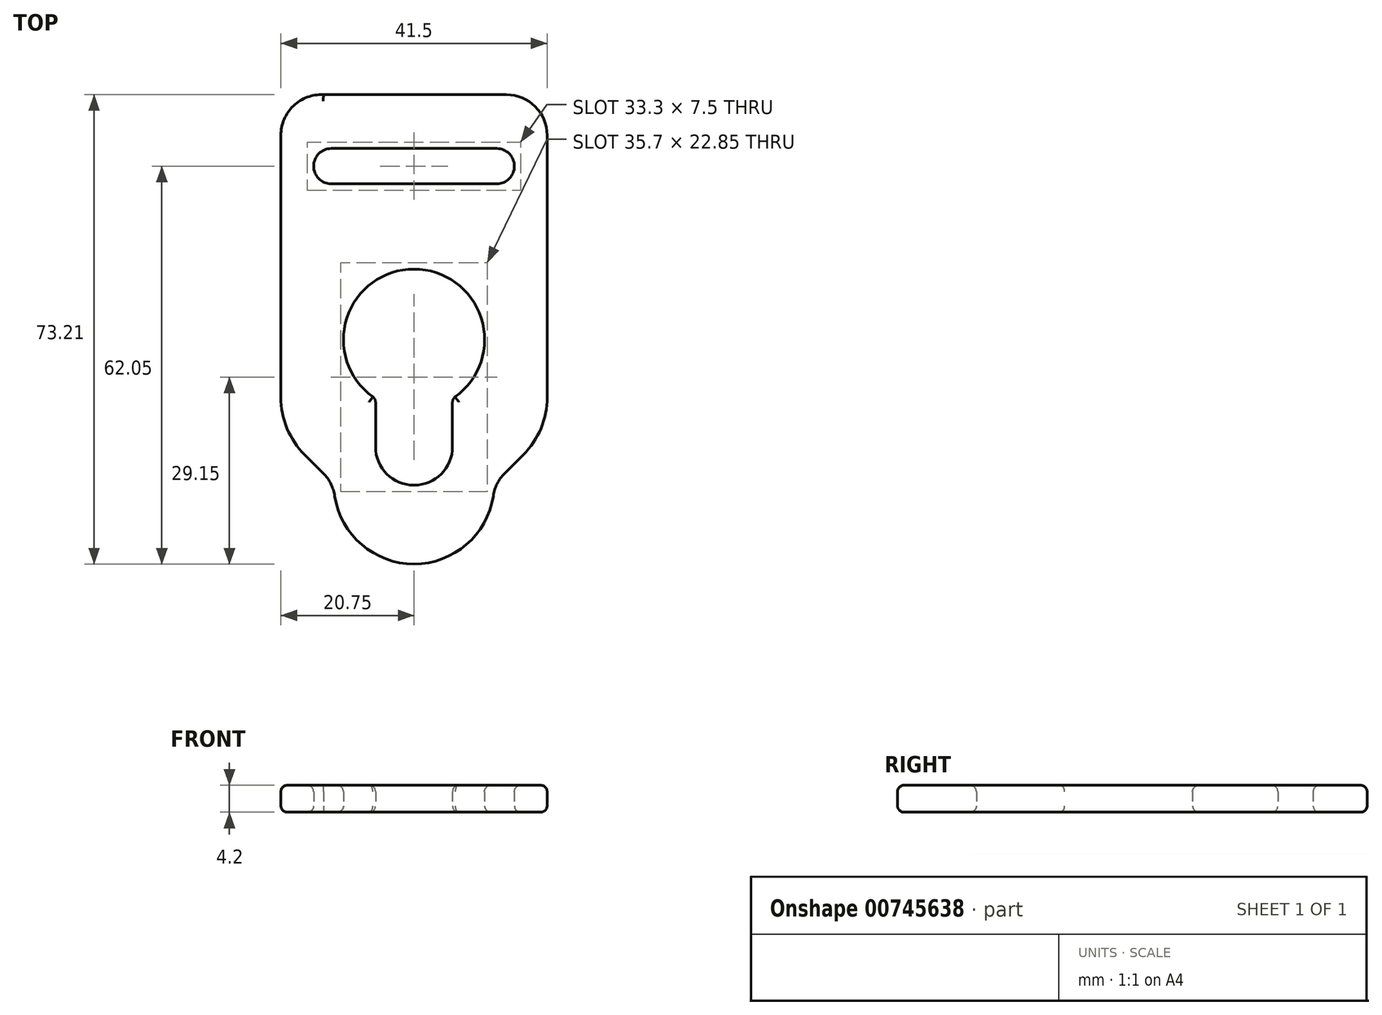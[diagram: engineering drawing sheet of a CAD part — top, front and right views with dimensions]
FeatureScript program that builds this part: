
annotation { "Feature Type Name" : "Feature", "Feature Type Description" : "" }
export const myFeature = defineFeature(function(context is Context, id is Id, definition is map)
    precondition{}
    {
        {
            var Q0;
            Q0=qCreatedBy(makeId("Top.planeOp"),FACE);
            var sketch = newSketch(context, id + "F0", { "sketchPlane" : qUnion([Q0])});
            skLineSegment(sketch, "E0.bottom", {"start": v(0, 0) * mm, "end": v(14.4, 0) * mm});
            skLineSegment(sketch, "E0.right", {"start": v(20.75, -6.35) * mm, "end": v(20.75, -47.19) * mm});
            skArc(sketch, "E1.filletArc", {"start": v(20.75, -6.35) * mm, "mid": v(18.9, -1.86) * mm, "end": v(14.4, 0) * mm});
            skArc(sketch, "E2", {"start": v(0, -73.2) * mm, "mid": v(8.14, -70.18) * mm, "end": v(12.36, -62.59) * mm});
            skLineSegment(sketch, "E3", {"start": v(14.14, -59.06) * mm, "end": v(17.03, -56.17) * mm});
            skArc(sketch, "E4.filletArc", {"start": v(17.03, -56.17) * mm, "mid": v(19.78, -52.05) * mm, "end": v(20.75, -47.19) * mm});
            skPoint(sketch, "E5.visualSharp", {"position": v(12.5, -60.7) * mm});
            skArc(sketch, "E5.filletArc", {"start": v(14.14, -59.06) * mm, "mid": v(12.97, -60.68) * mm, "end": v(12.36, -62.59) * mm});
            skArc(sketch, "E6", {"start": v(0, -60.9) * mm, "mid": v(4.24, -59.14) * mm, "end": v(6, -54.9) * mm});
            skLineSegment(sketch, "E7", {"start": v(6, -54.9) * mm, "end": v(6, -47.42) * mm});
            skArc(sketch, "E8.trimOffspring", {"start": v(6, -47.42) * mm, "mid": v(10.55, -35.07) * mm, "end": v(0, -27.2) * mm});
            skLineSegment(sketch, "E9.MirrorCS", {"start": v(-14.14, -59.06) * mm, "end": v(-17.03, -56.17) * mm});
            skArc(sketch, "E10.MirrorCS", {"start": v(-14.14, -59.06) * mm, "mid": v(-12.97, -60.68) * mm, "end": v(-12.36, -62.59) * mm});
            skArc(sketch, "E11.MirrorCS", {"start": v(-20.75, -6.35) * mm, "mid": v(-18.8, -1.76) * mm, "end": v(-14.12, 0) * mm});
            skArc(sketch, "E12.MirrorCS", {"start": v(-17.03, -56.17) * mm, "mid": v(-19.78, -52.05) * mm, "end": v(-20.75, -47.19) * mm});
            skArc(sketch, "E13.MirrorCS", {"start": v(0, -73.2) * mm, "mid": v(-8.14, -70.18) * mm, "end": v(-12.36, -62.59) * mm});
            skPoint(sketch, "E14.MirrorP", {"position": v(-12.5, -60.7) * mm});
            skArc(sketch, "E15.MirrorCS", {"start": v(0, -60.9) * mm, "mid": v(-4.24, -59.14) * mm, "end": v(-6, -54.9) * mm});
            skLineSegment(sketch, "E16.MirrorCS", {"start": v(0.28, 0) * mm, "end": v(-14.12, 0) * mm});
            skArc(sketch, "E17.MirrorCS", {"start": v(-6, -47.42) * mm, "mid": v(-10.55, -35.07) * mm, "end": v(0, -27.2) * mm});
            skLineSegment(sketch, "E18.MirrorCS", {"start": v(-6, -54.9) * mm, "end": v(-6, -47.42) * mm});
            skLineSegment(sketch, "E19.MirrorCS", {"start": v(-20.75, -6.35) * mm, "end": v(-20.75, -47.19) * mm});
            skLineSegment(sketch, "E20.bottom", {"start": v(-12.9, -8.4) * mm, "end": v(12.9, -8.4) * mm});
            skLineSegment(sketch, "E20.top", {"start": v(-12.9, -13.9) * mm, "end": v(12.9, -13.9) * mm});
            skLineSegment(sketch, "E20.left", {"start": v(-15.65, -11.15) * mm, "end": v(-15.65, -11.15) * mm});
            skLineSegment(sketch, "E20.right", {"start": v(15.65, -11.15) * mm, "end": v(15.65, -11.15) * mm});
            skPoint(sketch, "E21.visualSharp", {"position": v(-15.65, -13.9) * mm});
            skArc(sketch, "E21.filletArc", {"start": v(-15.65, -11.15) * mm, "mid": v(-14.84, -13.1) * mm, "end": v(-12.9, -13.9) * mm});
            skPoint(sketch, "E22.visualSharp", {"position": v(15.65, -13.9) * mm});
            skArc(sketch, "E22.filletArc", {"start": v(12.9, -13.9) * mm, "mid": v(14.84, -13.1) * mm, "end": v(15.65, -11.15) * mm});
            skPoint(sketch, "E23.visualSharp", {"position": v(-15.65, -8.4) * mm});
            skArc(sketch, "E23.filletArc", {"start": v(-12.9, -8.4) * mm, "mid": v(-14.84, -9.2) * mm, "end": v(-15.65, -11.15) * mm});
            skPoint(sketch, "E24.visualSharp", {"position": v(15.65, -8.4) * mm});
            skArc(sketch, "E24.filletArc", {"start": v(15.65, -11.15) * mm, "mid": v(14.84, -9.2) * mm, "end": v(12.9, -8.4) * mm});
            skSolve(sketch);
        }
        {
            var Q0;
            Q0=makeQuery(id+"F0.imprint","IMPRINT",FACE,{"disambiguationData":[TD([[makeQuery(id+"F0.imprint","IMPRINT",EDGE,{"derivedFrom":sQuery(id+"F0.wireOp",EDGE,"E0.bottom")}),-1.0]])]});
            extrude(context, id + "F1", {"entities" : qUnion([Q0]), "depth" : 4.2 * mm, "offsetDistance" : 25 * mm});
        }
        {
            var Q0;
            Q0=makeQuery(id+"F1.opExtrude","CAP_EDGE",EDGE,{"disambiguationData":[OSD([sQuery(id+"F0.wireOp",EDGE,"E0.right")])],"isStart":false});
            var Q1;
            Q1=makeQuery(id+"F1.opExtrude","CAP_EDGE",EDGE,{"disambiguationData":[OSD([sQuery(id+"F0.wireOp",EDGE,"E0.right")])],"isStart":true});
            var Q2;
            Q2=makeQuery(id+"F1.opExtrude","CAP_EDGE",EDGE,{"disambiguationData":[OSD([sQuery(id+"F0.wireOp",EDGE,"E8.trimOffspring"),sQuery(id+"F0.wireOp",EDGE,"E17.MirrorCS")])],"isStart":false});
            var Q3;
            Q3=makeQuery(id+"F1.opExtrude","CAP_EDGE",EDGE,{"disambiguationData":[OSD([sQuery(id+"F0.wireOp",EDGE,"E18.MirrorCS")])],"isStart":false});
            var Q4;
            Q4=makeQuery(id+"F1.opExtrude","CAP_EDGE",EDGE,{"disambiguationData":[OSD([sQuery(id+"F0.wireOp",EDGE,"E8.trimOffspring"),sQuery(id+"F0.wireOp",EDGE,"E17.MirrorCS")])],"isStart":true});
            var Q5;
            Q5=makeQuery(id+"F1.opExtrude","CAP_EDGE",EDGE,{"disambiguationData":[OSD([sQuery(id+"F0.wireOp",EDGE,"E18.MirrorCS")])],"isStart":true});
            var Q6;
            Q6=makeQuery(id+"F1.opExtrude","SWEPT_EDGE",EDGE,{"disambiguationData":[OSD([sQuery(id+"F0.wireOp",EDGE,"E17.MirrorCS"),sQuery(id+"F0.wireOp",EDGE,"E18.MirrorCS")])]});
            var Q7;
            Q7=makeQuery(id+"F1.opExtrude","SWEPT_EDGE",EDGE,{"disambiguationData":[OSD([sQuery(id+"F0.wireOp",EDGE,"E7"),sQuery(id+"F0.wireOp",EDGE,"E8.trimOffspring")])]});
            var Q8;
            Q8=makeQuery(id+"F1.opExtrude","CAP_EDGE",EDGE,{"disambiguationData":[OSD([sQuery(id+"F0.wireOp",EDGE,"E20.bottom")])],"isStart":false});
            var Q9;
            Q9=makeQuery(id+"F1.opExtrude","CAP_EDGE",EDGE,{"disambiguationData":[OSD([sQuery(id+"F0.wireOp",EDGE,"E20.bottom")])],"isStart":true});
            fillet(context, id + "F2", {"entities" : qUnion([Q0, Q1, Q2, Q3, Q4, Q5, Q6, Q7, Q8, Q9]), "radius" : 1 * mm, "tangentPropagation" : true, "allowEdgeOverflow" : false});
        }
    });
